# Revit family: Runtal R2F-1
name_source: partatom
category: Mechanical Equipment
revit_build: Autodesk Revit Architecture 2015 (Build: 20140606_1530(x64)
units: mm (PartAtom-declared; Revit-internal decimal feet)

## types (1)
- Radiator-R2F_1-Runtal-Commercial
    Actual Length = 508 mm  [stored 1.66667 ft]
    Assembly Code = D3020
    Casing = Powder Coated-Runtal-W-White
    Default Elevation = 1219.2 mm  [stored 4 ft]
    Description = R2F radiators are mounted horizontally and consist of two rows of fins sandwiched between two layers of panels.
    Fin Height = 67 mm
    Fin Length = 431.8 mm  [stored 1.41667 ft]
    Frame = UHMW, White
    Grille = Yes
    Grille Visibility = Yes
    Height = 144.78 mm  [stored 0.475 ft]
    Lamelle = Yes
    Length = 508 mm  [stored 1.66667 ft]
    Logo = Paint-Runtal-B-Black Matte
    Manufacturer = Runtal Radiators
    Model = R2F-1
    URL = http://www.runtalnorthamerica.com

note: [stored X ft] marks values corroborated as IEEE doubles in the binary element streams (Revit-internal decimal feet)

## geometry (parser evidence)
native form markers: Blend x18, Sweep x15
no freeform markers — native parametric forms only
